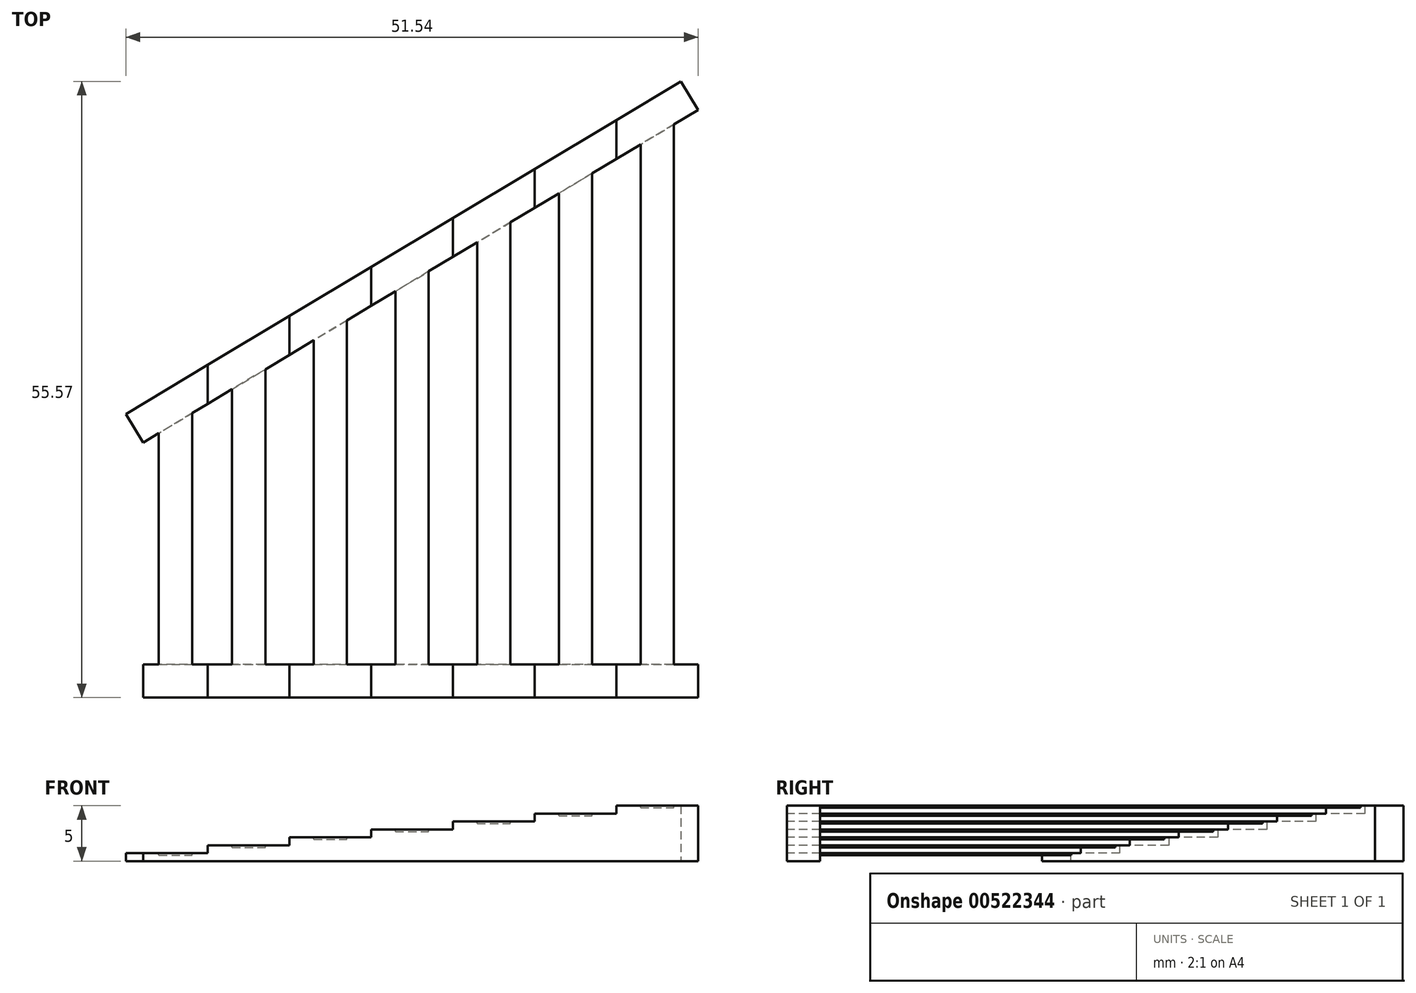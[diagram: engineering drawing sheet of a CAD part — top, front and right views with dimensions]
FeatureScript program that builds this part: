
annotation { "Feature Type Name" : "Feature", "Feature Type Description" : "" }
export const myFeature = defineFeature(function(context is Context, id is Id, definition is map)
    precondition{}
    {
        {
            var Q0;
            Q0=qCreatedBy(makeId("Top.planeOp"),FACE);
            var sketch = newSketch(context, id + "F0", { "sketchPlane" : qUnion([Q0])});
            skLineSegment(sketch, "E0.bottom", {"start": v(25, -1.5) * mm, "end": v(-25, -1.5) * mm});
            skLineSegment(sketch, "E0.top", {"start": v(25, 1.5) * mm, "end": v(-25, 1.5) * mm});
            skLineSegment(sketch, "E0.left", {"start": v(25, -1.5) * mm, "end": v(25, 1.5) * mm});
            skLineSegment(sketch, "E0.right", {"start": v(-25, -1.5) * mm, "end": v(-25, 1.5) * mm});
            skPoint(sketch, "E0.middle", {"position": v(0, 0) * mm});
            skLineSegment(sketch, "E1", {"start": v(-25, 21.5) * mm, "end": v(25, 51.5) * mm, "construction": true});
            skLineSegment(sketch, "E2.bottom", {"start": v(-25, 21.5) * mm, "end": v(25, 51.5) * mm});
            skLineSegment(sketch, "E2.top", {"start": v(-26.54, 24.07) * mm, "end": v(23.46, 54.07) * mm});
            skLineSegment(sketch, "E2.left", {"start": v(-25, 21.5) * mm, "end": v(-26.54, 24.07) * mm});
            skLineSegment(sketch, "E2.right", {"start": v(25, 51.5) * mm, "end": v(23.46, 54.07) * mm});
            skSolve(sketch);
        }
        {
            var Q0;
            Q0=qSketchRegion(id+"F0",true);
            extrude(context, id + "F1", {"entities" : qUnion([Q0]), "depth" : 5 * mm, "offsetDistance" : 25 * mm});
        }
        {
            var Q0;
            Q0=makeQuery(id+"F1.opExtrude","SWEPT_FACE",FACE,{"disambiguationData":[OSD([sQuery(id+"F0.wireOp",EDGE,"E0.bottom")])]});
            var sketch = newSketch(context, id + "F2", { "sketchPlane" : qUnion([Q0])});
            skLineSegment(sketch, "E3", {"start": v(-26.54, 5) * mm, "end": v(-26.54, 0.71) * mm});
            skLineSegment(sketch, "E4", {"start": v(-26.54, 0.71) * mm, "end": v(-19.18, 0.71) * mm});
            skLineSegment(sketch, "E5", {"start": v(-19.18, 0.71) * mm, "end": v(-19.18, 1.43) * mm});
            skLineSegment(sketch, "E6", {"start": v(-19.18, 1.43) * mm, "end": v(-11.82, 1.43) * mm});
            skLineSegment(sketch, "E7", {"start": v(-11.82, 1.43) * mm, "end": v(-11.82, 2.14) * mm});
            skLineSegment(sketch, "E8", {"start": v(-11.82, 2.14) * mm, "end": v(-4.45, 2.14) * mm});
            skLineSegment(sketch, "E9", {"start": v(-4.45, 2.14) * mm, "end": v(-4.45, 2.86) * mm});
            skLineSegment(sketch, "E10", {"start": v(-4.45, 2.86) * mm, "end": v(2.9, 2.86) * mm});
            skLineSegment(sketch, "E11", {"start": v(2.9, 2.86) * mm, "end": v(2.9, 3.57) * mm});
            skLineSegment(sketch, "E12", {"start": v(2.9, 3.57) * mm, "end": v(10.27, 3.57) * mm});
            skLineSegment(sketch, "E13", {"start": v(10.27, 3.57) * mm, "end": v(10.27, 4.29) * mm});
            skLineSegment(sketch, "E14", {"start": v(10.27, 4.29) * mm, "end": v(17.64, 4.29) * mm});
            skLineSegment(sketch, "E15", {"start": v(17.64, 4.29) * mm, "end": v(17.64, 5) * mm});
            skLineSegment(sketch, "E16", {"start": v(-26.54, 5) * mm, "end": v(17.64, 5) * mm});
            skLineSegment(sketch, "E17", {"start": v(-22.86, 0.71) * mm, "end": v(-22.86, 0) * mm, "construction": true});
            skLineSegment(sketch, "E18", {"start": v(17.64, 4.64) * mm, "end": v(25, 4.64) * mm, "construction": true});
            skSolve(sketch);
        }
        {
            var Q0;
            Q0=qSketchRegion(id+"F2",true);
            extrude(context, id + "F3", {"entities" : qUnion([Q0]), "operationType" : NewBodyOperationType.REMOVE, "endBound" : BoundingType.THROUGH_ALL, "oppositeDirection" : true, "depth" : 25 * mm, "offsetDistance" : 25 * mm});
        }
        {
            var Q0;
            Q0=makeQuery(id+"F1.opExtrude","SWEPT_FACE",FACE,{"disambiguationData":[OSD([sQuery(id+"F0.wireOp",EDGE,"E0.bottom")])]});
            var sketch = newSketch(context, id + "F4", { "sketchPlane" : qUnion([Q0])});
            skLineSegment(sketch, "E19.bottom", {"start": v(-23.6, 0.51) * mm, "end": v(-20.6, 0.51) * mm});
            skLineSegment(sketch, "E19.top", {"start": v(-23.6, 0.71) * mm, "end": v(-20.6, 0.71) * mm});
            skLineSegment(sketch, "E19.left", {"start": v(-23.6, 0.51) * mm, "end": v(-23.6, 0.71) * mm});
            skLineSegment(sketch, "E19.right", {"start": v(-20.6, 0.51) * mm, "end": v(-20.6, 0.71) * mm});
            skLineSegment(sketch, "E20.bottom", {"start": v(-17, 1.23) * mm, "end": v(-14, 1.23) * mm});
            skLineSegment(sketch, "E20.top", {"start": v(-17, 1.43) * mm, "end": v(-14, 1.43) * mm});
            skLineSegment(sketch, "E20.left", {"start": v(-17, 1.23) * mm, "end": v(-17, 1.43) * mm});
            skLineSegment(sketch, "E20.right", {"start": v(-14, 1.23) * mm, "end": v(-14, 1.43) * mm});
            skLineSegment(sketch, "E21.bottom", {"start": v(-9.64, 1.94) * mm, "end": v(-6.64, 1.94) * mm});
            skLineSegment(sketch, "E21.top", {"start": v(-9.64, 2.14) * mm, "end": v(-6.64, 2.14) * mm});
            skLineSegment(sketch, "E21.left", {"start": v(-9.64, 1.94) * mm, "end": v(-9.64, 2.14) * mm});
            skLineSegment(sketch, "E21.right", {"start": v(-6.64, 1.94) * mm, "end": v(-6.64, 2.14) * mm});
            skLineSegment(sketch, "E22.bottom", {"start": v(-2.27, 2.66) * mm, "end": v(0.73, 2.66) * mm});
            skLineSegment(sketch, "E22.top", {"start": v(-2.27, 2.86) * mm, "end": v(0.73, 2.86) * mm});
            skLineSegment(sketch, "E22.left", {"start": v(-2.27, 2.66) * mm, "end": v(-2.27, 2.86) * mm});
            skLineSegment(sketch, "E22.right", {"start": v(0.73, 2.66) * mm, "end": v(0.73, 2.86) * mm});
            skLineSegment(sketch, "E23.bottom", {"start": v(5.1, 3.37) * mm, "end": v(8.1, 3.37) * mm});
            skLineSegment(sketch, "E23.top", {"start": v(5.1, 3.57) * mm, "end": v(8.1, 3.57) * mm});
            skLineSegment(sketch, "E23.left", {"start": v(5.1, 3.37) * mm, "end": v(5.1, 3.57) * mm});
            skLineSegment(sketch, "E23.right", {"start": v(8.1, 3.37) * mm, "end": v(8.1, 3.57) * mm});
            skLineSegment(sketch, "E24.bottom", {"start": v(12.45, 4.09) * mm, "end": v(15.45, 4.09) * mm});
            skLineSegment(sketch, "E24.top", {"start": v(12.45, 4.29) * mm, "end": v(15.45, 4.29) * mm});
            skLineSegment(sketch, "E24.left", {"start": v(12.45, 4.09) * mm, "end": v(12.45, 4.29) * mm});
            skLineSegment(sketch, "E24.right", {"start": v(15.45, 4.09) * mm, "end": v(15.45, 4.29) * mm});
            skLineSegment(sketch, "E25.bottom", {"start": v(19.82, 4.8) * mm, "end": v(22.82, 4.8) * mm});
            skLineSegment(sketch, "E25.top", {"start": v(19.82, 5) * mm, "end": v(22.82, 5) * mm});
            skLineSegment(sketch, "E25.left", {"start": v(19.82, 4.8) * mm, "end": v(19.82, 5) * mm});
            skLineSegment(sketch, "E25.right", {"start": v(22.82, 4.8) * mm, "end": v(22.82, 5) * mm});
            skPoint(sketch, "E26", {"position": v(21.32, 5) * mm});
            skPoint(sketch, "E27", {"position": v(-22.1, 0.71) * mm});
            skPoint(sketch, "E28", {"position": v(-15.5, 1.43) * mm});
            skPoint(sketch, "E29", {"position": v(-8.14, 2.14) * mm});
            skPoint(sketch, "E30", {"position": v(-0.77, 2.86) * mm});
            skPoint(sketch, "E31", {"position": v(6.6, 3.57) * mm});
            skPoint(sketch, "E32", {"position": v(13.95, 4.29) * mm});
            skSolve(sketch);
        }
        {
            var Q0;
            Q0=qSketchRegion(id+"F4",true);
            var Q1;
            Q1=makeQuery(id+"F1.opExtrude","SWEPT_FACE",FACE,{"disambiguationData":[OSD([sQuery(id+"F0.wireOp",EDGE,"E2.top")])]});
            var Q2;
            Q2=makeQuery(id+"F1.opExtrude","SWEPT_BODY",BODY,{"disambiguationData":[OSD([sQuery(id+"F0.wireOp",EDGE,"E2.bottom"),sQuery(id+"F0.wireOp",EDGE,"E2.top"),sQuery(id+"F0.wireOp",EDGE,"E2.left"),sQuery(id+"F0.wireOp",EDGE,"E2.right")])]});
            extrude(context, id + "F5", {"entities" : qUnion([Q0]), "operationType" : NewBodyOperationType.ADD, "endBound" : BoundingType.UP_TO_SURFACE, "oppositeDirection" : true, "depth" : 25 * mm, "endBoundEntityFace" : qUnion([Q1]), "endBoundEntityBody" : qUnion([Q2]), "offsetDistance" : 25 * mm});
        }
    });
